# Revit family: 7.Фреоновый охладитель для прямоугольных каналов FLO
name_source: partatom
category: Оборудование
revit_build: Autodesk Revit 2016 (Build: 20151209_0715(x64)
units: mm (PartAtom-declared; Revit-internal decimal feet)

## family parameters
Всегда вертикально = Да
На основе рабочей плоскости = Нет
Общий = Нет
При загрузке вырезать с полостями = Нет
Размер круглого соединителя = Использовать диаметр
Тип детали = Нормальный
Точка расчета площади = Нет

## types (9) — shared parameters
d1 = 11 мм
Единица измерения = шт.
Завод изготовитель = KORF
К = 306 мм
Ключевая пометка = Вентиляция
Материал = Сталь серая
Наименование и тех.хар-ка = Фреоновый охладитель для прямоугольных каналов
Раздел = ОВ

## per-type parameters (varying)
| type | d | А | Б | Высота | Г | Д | Е | Ж | З | Заправочный объем, л | И | Масса единицы | Размер В | Тип, марка, обозначение | Холодопроизводительность, кВт | Ширина |
| 40-20 | 25 мм | 564 мм | 283 мм | 200 мм | 420 мм | 95 мм | 45 мм | 12 мм | 16 мм | 1 м³ | 730 мм | 16 кг | 317 мм | FLO 40-20 | 5.6 | 400 мм |
| 50-25 | 25 мм | 664 мм | 333 мм | 250 мм | 520 мм | 125 мм | 50 мм | 12 мм | 16 мм | 1.4 м³ | 830 мм | 18 кг | 270 мм | FLO 50-25 | 9 | 500 мм |
| 50-30 | 25 мм | 664 мм | 383 мм | 300 мм | 520 мм | 155 мм | 50 мм | 16 мм | 22 мм | 1.8 м³ | 830 мм | 19 кг | 320 мм | FLO 50-30 | 10.6 | 500 мм |
| 60-30 | 25 мм | 764 мм | 383 мм | 300 мм | 620 мм | 155 мм | 60 мм | 16 мм | 22 мм | 2 м³ | 930 мм | 21 кг | 320 мм | FLO 60-30 | 12.9 | 600 мм |
| 60-35 | 25 мм | 764 мм | 433 мм | 350 мм | 620 мм | 195 мм | 45 мм | 16 мм | 22 мм | 2.3 м³ | 930 мм | 23 кг | 370 мм | FLO 60-35 | 15.1 | 600 мм |
| 70-40 | 25 мм | 864 мм | 483 мм | 400 мм | 720 мм | 220 мм | 40 мм | 22 мм | 28 мм | 3 м³ | 1030 мм | 26 кг | 420 мм | FLO 70-40 | 20.2 | 700 мм |
| 80-50 | 25 мм | 964 мм | 583 мм | 500 мм | 820 мм | 290 мм | 53 мм | 22 мм | 28 мм | 4.4 м³ | 1130 мм | 32 кг | 520 мм | FLO 80-50 | 28.5 | 800 мм |
| 90-50 | 25 мм | 1074 мм | 598 мм | 500 мм | 930 мм | 330 мм | 55 мм | 28 мм | 35 мм | 4.8 м³ | 1240 мм | 36 кг | 530 мм | FLO 90-50 | 32 | 900 мм |
| 100-50 | 38 мм | 1174 мм | 598 мм | 500 мм | 1030 мм | 330 мм | 55 мм | 28 мм | 35 мм | 5.3 м³ | 1340 мм | 42 кг | 530 мм | FLO 100-50 | 35.5 | 1000 мм |
